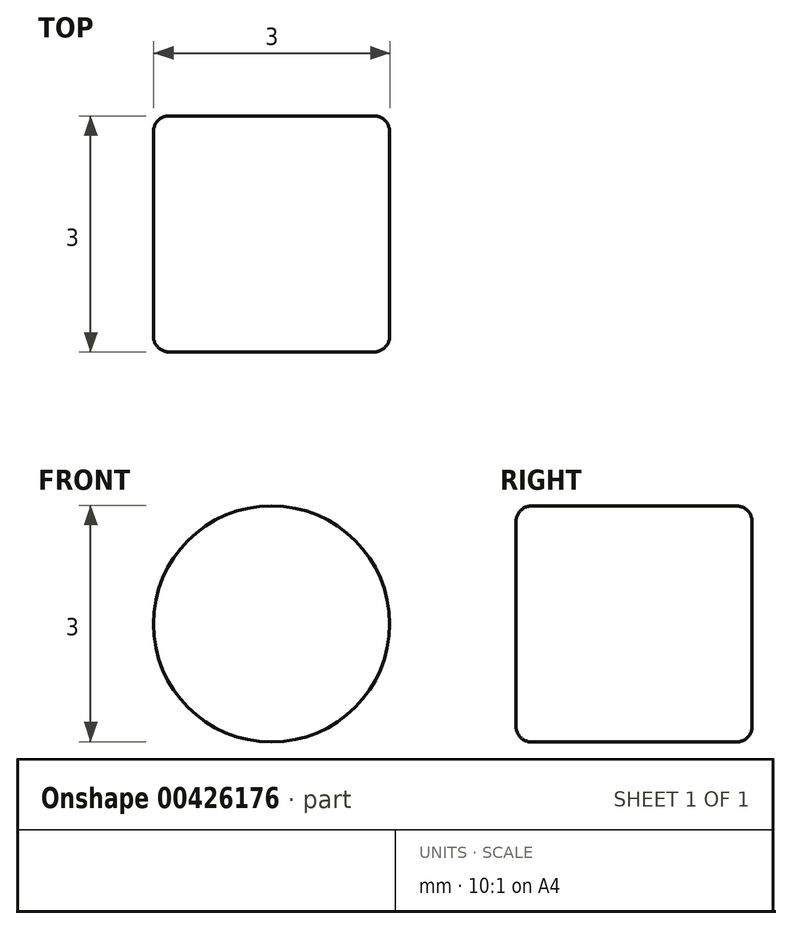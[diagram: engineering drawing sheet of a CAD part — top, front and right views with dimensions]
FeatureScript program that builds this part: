
annotation { "Feature Type Name" : "Feature", "Feature Type Description" : "" }
export const myFeature = defineFeature(function(context is Context, id is Id, definition is map)
    precondition{}
    {
        {
            var Q0;
            Q0=qCreatedBy(makeId("Front.planeOp"),FACE);
            var sketch = newSketch(context, id + "F0", { "sketchPlane" : qUnion([Q0])});
            skCircle(sketch, "E0", {"center": v(-5.4, 45.42) * mm, "radius": 1.5 * mm});
            skCircle(sketch, "E1", {"center": v(-26.87, 2.37) * mm, "radius": 1.5 * mm});
            skCircle(sketch, "E2", {"center": v(-18.87, 2.37) * mm, "radius": 1.5 * mm});
            skCircle(sketch, "E3", {"center": v(-8.9, 45.42) * mm, "radius": 1.5 * mm});
            skCircle(sketch, "E4", {"center": v(-12.4, 45.42) * mm, "radius": 1.5 * mm});
            skLineSegment(sketch, "E5", {"start": v(-28.2, 0) * mm, "end": v(-17.78, 0) * mm});
            skLineSegment(sketch, "E6", {"start": v(-29.7, 1.5) * mm, "end": v(-29.7, 15.65) * mm});
            skLineSegment(sketch, "E7", {"start": v(-26.81, 30.44) * mm, "end": v(-26.22, 31.9) * mm});
            skLineSegment(sketch, "E8", {"start": v(-20.6, 41.55) * mm, "end": v(-16.06, 47.28) * mm});
            skLineSegment(sketch, "E9", {"start": v(-16.28, 1.5) * mm, "end": v(-16.28, 10.93) * mm});
            skLineSegment(sketch, "E10", {"start": v(-13.7, 48.42) * mm, "end": v(-5.4, 48.42) * mm});
            skArc(sketch, "E11", {"start": v(-16.28, 10.93) * mm, "mid": v(-15.59, 18.3) * mm, "end": v(-13.53, 25.4) * mm});
            skArc(sketch, "E12", {"start": v(-13.53, 25.4) * mm, "mid": v(-11.6, 29.4) * mm, "end": v(-9.22, 33.16) * mm});
            skArc(sketch, "E13", {"start": v(-29.7, 15.65) * mm, "mid": v(-28.97, 23.18) * mm, "end": v(-26.81, 30.44) * mm});
            skArc(sketch, "E14", {"start": v(-26.22, 31.9) * mm, "mid": v(-23.75, 36.93) * mm, "end": v(-20.6, 41.55) * mm});
            skCircle(sketch, "E15", {"center": v(-5.4, 41.42) * mm, "radius": 1.5 * mm});
            skCircle(sketch, "E16", {"center": v(-8.9, 41.42) * mm, "radius": 1.5 * mm});
            skCircle(sketch, "E17", {"center": v(-12.4, 41.42) * mm, "radius": 1.5 * mm});
            skCircle(sketch, "E18", {"center": v(-5.4, 37.42) * mm, "radius": 1.5 * mm});
            skCircle(sketch, "E19", {"center": v(-8.9, 37.42) * mm, "radius": 1.5 * mm});
            skCircle(sketch, "E20", {"center": v(-12.4, 37.42) * mm, "radius": 1.5 * mm});
            skLineSegment(sketch, "E21", {"start": v(-2.4, 45.42) * mm, "end": v(-2.4, 37.42) * mm});
            skLineSegment(sketch, "E22", {"start": v(-5.4, 34.42) * mm, "end": v(-6.78, 34.42) * mm});
            skArc(sketch, "E23", {"start": v(-5.4, 48.42) * mm, "mid": v(-3.28, 47.54) * mm, "end": v(-2.4, 45.42) * mm});
            skArc(sketch, "E24", {"start": v(-2.4, 37.42) * mm, "mid": v(-3.28, 35.3) * mm, "end": v(-5.4, 34.42) * mm});
            skArc(sketch, "E25", {"start": v(-16.06, 47.28) * mm, "mid": v(-15.01, 48.12) * mm, "end": v(-13.7, 48.42) * mm});
            skArc(sketch, "E26", {"start": v(-9.22, 33.16) * mm, "mid": v(-8.15, 34.08) * mm, "end": v(-6.78, 34.42) * mm});
            skArc(sketch, "E27", {"start": v(-29.7, 1.5) * mm, "mid": v(-29.25, 0.44) * mm, "end": v(-28.2, 0) * mm});
            skArc(sketch, "E28", {"start": v(-17.78, 0) * mm, "mid": v(-16.72, 0.44) * mm, "end": v(-16.28, 1.5) * mm});
            skLineSegment(sketch, "E29", {"start": v(-20.28, 9.5) * mm, "end": v(-20.28, 10.93) * mm});
            skLineSegment(sketch, "E30", {"start": v(-24.2, 8) * mm, "end": v(-21.78, 8) * mm});
            skArc(sketch, "E31", {"start": v(-25.7, 9.5) * mm, "mid": v(-25.25, 8.44) * mm, "end": v(-24.2, 8) * mm});
            skArc(sketch, "E32", {"start": v(-21.78, 8) * mm, "mid": v(-20.72, 8.44) * mm, "end": v(-20.28, 9.5) * mm});
            skLineSegment(sketch, "E33", {"start": v(-25.7, 10.93) * mm, "end": v(-25.7, 9.5) * mm});
            skLineSegment(sketch, "E34", {"start": v(-21.78, 12.43) * mm, "end": v(-24.2, 12.43) * mm});
            skArc(sketch, "E35", {"start": v(-20.28, 10.93) * mm, "mid": v(-20.72, 12) * mm, "end": v(-21.78, 12.43) * mm});
            skArc(sketch, "E36", {"start": v(-24.2, 12.43) * mm, "mid": v(-25.25, 12) * mm, "end": v(-25.7, 10.93) * mm});
            skLineSegment(sketch, "E37", {"start": v(-16.01, 29.94) * mm, "end": v(-16.01, 30.49) * mm});
            skLineSegment(sketch, "E38", {"start": v(-19.14, 28.44) * mm, "end": v(-17.51, 28.44) * mm});
            skLineSegment(sketch, "E39", {"start": v(-20.64, 30.49) * mm, "end": v(-20.64, 29.94) * mm});
            skLineSegment(sketch, "E40", {"start": v(-17.51, 31.99) * mm, "end": v(-19.14, 31.99) * mm});
            skLineSegment(sketch, "E41", {"start": v(-19.08, 19.72) * mm, "end": v(-19.08, 20.7) * mm});
            skLineSegment(sketch, "E42", {"start": v(-22.45, 18.22) * mm, "end": v(-20.58, 18.22) * mm});
            skLineSegment(sketch, "E43", {"start": v(-23.95, 20.7) * mm, "end": v(-23.95, 19.72) * mm});
            skLineSegment(sketch, "E44", {"start": v(-20.58, 22.2) * mm, "end": v(-22.45, 22.2) * mm});
            skArc(sketch, "E45.filletArc", {"start": v(-19.14, 31.99) * mm, "mid": v(-20.2, 31.55) * mm, "end": v(-20.64, 30.49) * mm});
            skArc(sketch, "E46.filletArc", {"start": v(-16.01, 30.49) * mm, "mid": v(-16.45, 31.55) * mm, "end": v(-17.51, 31.99) * mm});
            skArc(sketch, "E47.filletArc", {"start": v(-17.51, 28.44) * mm, "mid": v(-16.45, 28.88) * mm, "end": v(-16.01, 29.94) * mm});
            skArc(sketch, "E48.filletArc", {"start": v(-20.64, 29.94) * mm, "mid": v(-20.2, 28.88) * mm, "end": v(-19.14, 28.44) * mm});
            skArc(sketch, "E49.filletArc", {"start": v(-22.45, 22.2) * mm, "mid": v(-23.51, 21.77) * mm, "end": v(-23.95, 20.7) * mm});
            skArc(sketch, "E50.filletArc", {"start": v(-19.08, 20.7) * mm, "mid": v(-19.52, 21.77) * mm, "end": v(-20.58, 22.2) * mm});
            skArc(sketch, "E51.filletArc", {"start": v(-20.58, 18.22) * mm, "mid": v(-19.52, 18.66) * mm, "end": v(-19.08, 19.72) * mm});
            skArc(sketch, "E52.filletArc", {"start": v(-23.95, 19.72) * mm, "mid": v(-23.51, 18.66) * mm, "end": v(-22.45, 18.22) * mm});
            skArc(sketch, "E53.MirrorCS", {"start": v(29.7, 1.5) * mm, "mid": v(29.25, 0.44) * mm, "end": v(28.2, 0) * mm});
            skLineSegment(sketch, "E54.MirrorCS", {"start": v(23.95, 20.7) * mm, "end": v(23.95, 19.72) * mm});
            skArc(sketch, "E55.MirrorCS", {"start": v(22.45, 22.2) * mm, "mid": v(23.51, 21.77) * mm, "end": v(23.95, 20.7) * mm});
            skLineSegment(sketch, "E56.MirrorCS", {"start": v(25.7, 10.93) * mm, "end": v(25.7, 9.5) * mm});
            skLineSegment(sketch, "E57.MirrorCS", {"start": v(16.01, 29.94) * mm, "end": v(16.01, 30.49) * mm});
            skLineSegment(sketch, "E58.MirrorCS", {"start": v(5.4, 34.42) * mm, "end": v(6.78, 34.42) * mm});
            skLineSegment(sketch, "E59.MirrorCS", {"start": v(19.14, 28.44) * mm, "end": v(17.51, 28.44) * mm});
            skLineSegment(sketch, "E60.MirrorCS", {"start": v(20.64, 30.49) * mm, "end": v(20.64, 29.94) * mm});
            skLineSegment(sketch, "E61.MirrorCS", {"start": v(21.78, 12.43) * mm, "end": v(24.2, 12.43) * mm});
            skLineSegment(sketch, "E62.MirrorCS", {"start": v(17.51, 31.99) * mm, "end": v(19.14, 31.99) * mm});
            skLineSegment(sketch, "E63.MirrorCS", {"start": v(19.08, 19.72) * mm, "end": v(19.08, 20.7) * mm});
            skArc(sketch, "E64.MirrorCS", {"start": v(16.06, 47.28) * mm, "mid": v(15.01, 48.12) * mm, "end": v(13.7, 48.42) * mm});
            skLineSegment(sketch, "E65.MirrorCS", {"start": v(22.45, 18.22) * mm, "end": v(20.58, 18.22) * mm});
            skArc(sketch, "E66.MirrorCS", {"start": v(9.22, 33.16) * mm, "mid": v(8.15, 34.08) * mm, "end": v(6.78, 34.42) * mm});
            skArc(sketch, "E67.MirrorCS", {"start": v(19.14, 31.99) * mm, "mid": v(20.2, 31.55) * mm, "end": v(20.64, 30.49) * mm});
            skLineSegment(sketch, "E68.MirrorCS", {"start": v(26.81, 30.44) * mm, "end": v(26.22, 31.9) * mm});
            skLineSegment(sketch, "E69.MirrorCS", {"start": v(20.28, 9.5) * mm, "end": v(20.28, 10.93) * mm});
            skLineSegment(sketch, "E70.MirrorCS", {"start": v(20.58, 22.2) * mm, "end": v(22.45, 22.2) * mm});
            skArc(sketch, "E71.MirrorCS", {"start": v(17.78, 0) * mm, "mid": v(16.72, 0.44) * mm, "end": v(16.28, 1.5) * mm});
            skArc(sketch, "E72.MirrorCS", {"start": v(16.01, 30.49) * mm, "mid": v(16.45, 31.55) * mm, "end": v(17.51, 31.99) * mm});
            skLineSegment(sketch, "E73.MirrorCS", {"start": v(24.2, 8) * mm, "end": v(21.78, 8) * mm});
            skArc(sketch, "E74.MirrorCS", {"start": v(17.51, 28.44) * mm, "mid": v(16.45, 28.88) * mm, "end": v(16.01, 29.94) * mm});
            skArc(sketch, "E75.MirrorCS", {"start": v(25.7, 9.5) * mm, "mid": v(25.25, 8.44) * mm, "end": v(24.2, 8) * mm});
            skArc(sketch, "E76.MirrorCS", {"start": v(24.2, 12.43) * mm, "mid": v(25.25, 12) * mm, "end": v(25.7, 10.93) * mm});
            skArc(sketch, "E77.MirrorCS", {"start": v(20.28, 10.93) * mm, "mid": v(20.72, 12) * mm, "end": v(21.78, 12.43) * mm});
            skArc(sketch, "E78.MirrorCS", {"start": v(20.64, 29.94) * mm, "mid": v(20.2, 28.88) * mm, "end": v(19.14, 28.44) * mm});
            skArc(sketch, "E79.MirrorCS", {"start": v(23.95, 19.72) * mm, "mid": v(23.51, 18.66) * mm, "end": v(22.45, 18.22) * mm});
            skArc(sketch, "E80.MirrorCS", {"start": v(21.78, 8) * mm, "mid": v(20.72, 8.44) * mm, "end": v(20.28, 9.5) * mm});
            skCircle(sketch, "E81.MirrorC", {"center": v(12.4, 41.42) * mm, "radius": 1.5 * mm});
            skLineSegment(sketch, "E82.MirrorCS", {"start": v(2.4, 45.42) * mm, "end": v(2.4, 37.42) * mm});
            skCircle(sketch, "E83.MirrorC", {"center": v(5.4, 37.42) * mm, "radius": 1.5 * mm});
            skArc(sketch, "E84.MirrorCS", {"start": v(19.08, 20.7) * mm, "mid": v(19.52, 21.77) * mm, "end": v(20.58, 22.2) * mm});
            skArc(sketch, "E85.MirrorCS", {"start": v(5.4, 48.42) * mm, "mid": v(3.28, 47.54) * mm, "end": v(2.4, 45.42) * mm});
            skArc(sketch, "E86.MirrorCS", {"start": v(2.4, 37.42) * mm, "mid": v(3.28, 35.3) * mm, "end": v(5.4, 34.42) * mm});
            skLineSegment(sketch, "E87.MirrorCS", {"start": v(29.7, 1.5) * mm, "end": v(29.7, 15.65) * mm});
            skLineSegment(sketch, "E88.MirrorCS", {"start": v(20.6, 41.55) * mm, "end": v(16.06, 47.28) * mm});
            skLineSegment(sketch, "E89.MirrorCS", {"start": v(16.28, 1.5) * mm, "end": v(16.28, 10.93) * mm});
            skLineSegment(sketch, "E90.MirrorCS", {"start": v(13.7, 48.42) * mm, "end": v(5.4, 48.42) * mm});
            skArc(sketch, "E91.MirrorCS", {"start": v(29.7, 15.65) * mm, "mid": v(28.97, 23.18) * mm, "end": v(26.81, 30.44) * mm});
            skArc(sketch, "E92.MirrorCS", {"start": v(26.22, 31.9) * mm, "mid": v(23.75, 36.93) * mm, "end": v(20.6, 41.55) * mm});
            skCircle(sketch, "E93.MirrorC", {"center": v(5.4, 41.42) * mm, "radius": 1.5 * mm});
            skArc(sketch, "E94.MirrorCS", {"start": v(16.28, 10.93) * mm, "mid": v(15.59, 18.3) * mm, "end": v(13.53, 25.4) * mm});
            skCircle(sketch, "E95.MirrorC", {"center": v(5.4, 45.42) * mm, "radius": 1.5 * mm});
            skCircle(sketch, "E96.MirrorC", {"center": v(26.87, 2.37) * mm, "radius": 1.5 * mm});
            skArc(sketch, "E97.MirrorCS", {"start": v(13.53, 25.4) * mm, "mid": v(11.6, 29.4) * mm, "end": v(9.22, 33.16) * mm});
            skCircle(sketch, "E98.MirrorC", {"center": v(18.87, 2.37) * mm, "radius": 1.5 * mm});
            skCircle(sketch, "E99.MirrorC", {"center": v(8.9, 45.42) * mm, "radius": 1.5 * mm});
            skCircle(sketch, "E100.MirrorC", {"center": v(12.4, 45.42) * mm, "radius": 1.5 * mm});
            skLineSegment(sketch, "E101.MirrorCS", {"start": v(28.2, 0) * mm, "end": v(17.78, 0) * mm});
            skCircle(sketch, "E102.MirrorC", {"center": v(8.9, 41.42) * mm, "radius": 1.5 * mm});
            skCircle(sketch, "E103.MirrorC", {"center": v(8.9, 37.42) * mm, "radius": 1.5 * mm});
            skArc(sketch, "E104.MirrorCS", {"start": v(20.58, 18.22) * mm, "mid": v(19.52, 18.66) * mm, "end": v(19.08, 19.72) * mm});
            skCircle(sketch, "E105.MirrorC", {"center": v(12.4, 37.42) * mm, "radius": 1.5 * mm});
            skSolve(sketch);
        }
        {
            var Q0;
            Q0=makeQuery(id+"F0.imprint","IMPRINT",FACE,{"disambiguationData":[TD([[makeQuery(id+"F0.imprint","IMPRINT",EDGE,{"derivedFrom":sQuery(id+"F0.wireOp",EDGE,"E0")}),1.0]])]});
            var Q1;
            Q1=makeQuery(id+"F0.imprint","IMPRINT",FACE,{"disambiguationData":[TD([[makeQuery(id+"F0.imprint","IMPRINT",EDGE,{"derivedFrom":sQuery(id+"F0.wireOp",EDGE,"E53.MirrorCS")}),-1.0]])]});
            extrude(context, id + "F1", {"entities" : qUnion([Q0, Q1]), "depth" : 3 * mm});
        }
        {
            var Q0;
            Q0=makeQuery(id+"F1.opExtrude","CAP_FACE",FACE,{"disambiguationData":[OSD([sQuery(id+"F0.wireOp",EDGE,"E0"),sQuery(id+"F0.wireOp",EDGE,"E1"),sQuery(id+"F0.wireOp",EDGE,"E2"),sQuery(id+"F0.wireOp",EDGE,"E3"),sQuery(id+"F0.wireOp",EDGE,"E4"),sQuery(id+"F0.wireOp",EDGE,"E5"),sQuery(id+"F0.wireOp",EDGE,"E6"),sQuery(id+"F0.wireOp",EDGE,"E7"),sQuery(id+"F0.wireOp",EDGE,"E8"),sQuery(id+"F0.wireOp",EDGE,"E9"),sQuery(id+"F0.wireOp",EDGE,"E10"),sQuery(id+"F0.wireOp",EDGE,"E11"),sQuery(id+"F0.wireOp",EDGE,"E12"),sQuery(id+"F0.wireOp",EDGE,"E13"),sQuery(id+"F0.wireOp",EDGE,"E14"),sQuery(id+"F0.wireOp",EDGE,"E15"),sQuery(id+"F0.wireOp",EDGE,"E16"),sQuery(id+"F0.wireOp",EDGE,"E17"),sQuery(id+"F0.wireOp",EDGE,"E18"),sQuery(id+"F0.wireOp",EDGE,"E19"),sQuery(id+"F0.wireOp",EDGE,"E20"),sQuery(id+"F0.wireOp",EDGE,"E21"),sQuery(id+"F0.wireOp",EDGE,"E22"),sQuery(id+"F0.wireOp",EDGE,"E23"),sQuery(id+"F0.wireOp",EDGE,"E24"),sQuery(id+"F0.wireOp",EDGE,"E25"),sQuery(id+"F0.wireOp",EDGE,"E26"),sQuery(id+"F0.wireOp",EDGE,"E27"),sQuery(id+"F0.wireOp",EDGE,"E28"),sQuery(id+"F0.wireOp",EDGE,"E29"),sQuery(id+"F0.wireOp",EDGE,"E30"),sQuery(id+"F0.wireOp",EDGE,"E31"),sQuery(id+"F0.wireOp",EDGE,"E32"),sQuery(id+"F0.wireOp",EDGE,"E33"),sQuery(id+"F0.wireOp",EDGE,"E34"),sQuery(id+"F0.wireOp",EDGE,"E35"),sQuery(id+"F0.wireOp",EDGE,"E36"),sQuery(id+"F0.wireOp",EDGE,"E37"),sQuery(id+"F0.wireOp",EDGE,"E38"),sQuery(id+"F0.wireOp",EDGE,"E39"),sQuery(id+"F0.wireOp",EDGE,"E40"),sQuery(id+"F0.wireOp",EDGE,"E41"),sQuery(id+"F0.wireOp",EDGE,"E42"),sQuery(id+"F0.wireOp",EDGE,"E43"),sQuery(id+"F0.wireOp",EDGE,"E44"),sQuery(id+"F0.wireOp",EDGE,"E45.filletArc"),sQuery(id+"F0.wireOp",EDGE,"E46.filletArc"),sQuery(id+"F0.wireOp",EDGE,"E47.filletArc"),sQuery(id+"F0.wireOp",EDGE,"E48.filletArc"),sQuery(id+"F0.wireOp",EDGE,"E49.filletArc"),sQuery(id+"F0.wireOp",EDGE,"E50.filletArc"),sQuery(id+"F0.wireOp",EDGE,"E51.filletArc"),sQuery(id+"F0.wireOp",EDGE,"E52.filletArc")])],"isStart":false});
            var Q1;
            Q1=makeQuery(id+"F1.opExtrude","CAP_FACE",FACE,{"disambiguationData":[OSD([sQuery(id+"F0.wireOp",EDGE,"E53.MirrorCS"),sQuery(id+"F0.wireOp",EDGE,"E54.MirrorCS"),sQuery(id+"F0.wireOp",EDGE,"E55.MirrorCS"),sQuery(id+"F0.wireOp",EDGE,"E56.MirrorCS"),sQuery(id+"F0.wireOp",EDGE,"E57.MirrorCS"),sQuery(id+"F0.wireOp",EDGE,"E58.MirrorCS"),sQuery(id+"F0.wireOp",EDGE,"E59.MirrorCS"),sQuery(id+"F0.wireOp",EDGE,"E60.MirrorCS"),sQuery(id+"F0.wireOp",EDGE,"E61.MirrorCS"),sQuery(id+"F0.wireOp",EDGE,"E62.MirrorCS"),sQuery(id+"F0.wireOp",EDGE,"E63.MirrorCS"),sQuery(id+"F0.wireOp",EDGE,"E64.MirrorCS"),sQuery(id+"F0.wireOp",EDGE,"E65.MirrorCS"),sQuery(id+"F0.wireOp",EDGE,"E66.MirrorCS"),sQuery(id+"F0.wireOp",EDGE,"E67.MirrorCS"),sQuery(id+"F0.wireOp",EDGE,"E68.MirrorCS"),sQuery(id+"F0.wireOp",EDGE,"E69.MirrorCS"),sQuery(id+"F0.wireOp",EDGE,"E70.MirrorCS"),sQuery(id+"F0.wireOp",EDGE,"E71.MirrorCS"),sQuery(id+"F0.wireOp",EDGE,"E72.MirrorCS"),sQuery(id+"F0.wireOp",EDGE,"E73.MirrorCS"),sQuery(id+"F0.wireOp",EDGE,"E74.MirrorCS"),sQuery(id+"F0.wireOp",EDGE,"E75.MirrorCS"),sQuery(id+"F0.wireOp",EDGE,"E76.MirrorCS"),sQuery(id+"F0.wireOp",EDGE,"E77.MirrorCS"),sQuery(id+"F0.wireOp",EDGE,"E78.MirrorCS"),sQuery(id+"F0.wireOp",EDGE,"E79.MirrorCS"),sQuery(id+"F0.wireOp",EDGE,"E80.MirrorCS"),sQuery(id+"F0.wireOp",EDGE,"E81.MirrorC"),sQuery(id+"F0.wireOp",EDGE,"E82.MirrorCS"),sQuery(id+"F0.wireOp",EDGE,"E83.MirrorC"),sQuery(id+"F0.wireOp",EDGE,"E84.MirrorCS"),sQuery(id+"F0.wireOp",EDGE,"E85.MirrorCS"),sQuery(id+"F0.wireOp",EDGE,"E86.MirrorCS"),sQuery(id+"F0.wireOp",EDGE,"E87.MirrorCS"),sQuery(id+"F0.wireOp",EDGE,"E88.MirrorCS"),sQuery(id+"F0.wireOp",EDGE,"E89.MirrorCS"),sQuery(id+"F0.wireOp",EDGE,"E90.MirrorCS"),sQuery(id+"F0.wireOp",EDGE,"E91.MirrorCS"),sQuery(id+"F0.wireOp",EDGE,"E92.MirrorCS"),sQuery(id+"F0.wireOp",EDGE,"E93.MirrorC"),sQuery(id+"F0.wireOp",EDGE,"E94.MirrorCS"),sQuery(id+"F0.wireOp",EDGE,"E95.MirrorC"),sQuery(id+"F0.wireOp",EDGE,"E96.MirrorC"),sQuery(id+"F0.wireOp",EDGE,"E97.MirrorCS"),sQuery(id+"F0.wireOp",EDGE,"E98.MirrorC"),sQuery(id+"F0.wireOp",EDGE,"E99.MirrorC"),sQuery(id+"F0.wireOp",EDGE,"E100.MirrorC"),sQuery(id+"F0.wireOp",EDGE,"E101.MirrorCS"),sQuery(id+"F0.wireOp",EDGE,"E102.MirrorC"),sQuery(id+"F0.wireOp",EDGE,"E103.MirrorC"),sQuery(id+"F0.wireOp",EDGE,"E104.MirrorCS"),sQuery(id+"F0.wireOp",EDGE,"E105.MirrorC")])],"isStart":false});
            fillet(context, id + "F2", {"entities" : qUnion([Q0, Q1]), "radius" : .2 * mm, "tangentPropagation" : true, "allowEdgeOverflow" : false});
        }
        {
            var Q0;
            Q0=makeQuery(id+"F1.opExtrude","CAP_FACE",FACE,{"disambiguationData":[OSD([sQuery(id+"F0.wireOp",EDGE,"E0"),sQuery(id+"F0.wireOp",EDGE,"E1"),sQuery(id+"F0.wireOp",EDGE,"E2"),sQuery(id+"F0.wireOp",EDGE,"E3"),sQuery(id+"F0.wireOp",EDGE,"E4"),sQuery(id+"F0.wireOp",EDGE,"E5"),sQuery(id+"F0.wireOp",EDGE,"E6"),sQuery(id+"F0.wireOp",EDGE,"E7"),sQuery(id+"F0.wireOp",EDGE,"E8"),sQuery(id+"F0.wireOp",EDGE,"E9"),sQuery(id+"F0.wireOp",EDGE,"E10"),sQuery(id+"F0.wireOp",EDGE,"E11"),sQuery(id+"F0.wireOp",EDGE,"E12"),sQuery(id+"F0.wireOp",EDGE,"E13"),sQuery(id+"F0.wireOp",EDGE,"E14"),sQuery(id+"F0.wireOp",EDGE,"E15"),sQuery(id+"F0.wireOp",EDGE,"E16"),sQuery(id+"F0.wireOp",EDGE,"E17"),sQuery(id+"F0.wireOp",EDGE,"E18"),sQuery(id+"F0.wireOp",EDGE,"E19"),sQuery(id+"F0.wireOp",EDGE,"E20"),sQuery(id+"F0.wireOp",EDGE,"E21"),sQuery(id+"F0.wireOp",EDGE,"E22"),sQuery(id+"F0.wireOp",EDGE,"E23"),sQuery(id+"F0.wireOp",EDGE,"E24"),sQuery(id+"F0.wireOp",EDGE,"E25"),sQuery(id+"F0.wireOp",EDGE,"E26"),sQuery(id+"F0.wireOp",EDGE,"E27"),sQuery(id+"F0.wireOp",EDGE,"E28"),sQuery(id+"F0.wireOp",EDGE,"E29"),sQuery(id+"F0.wireOp",EDGE,"E30"),sQuery(id+"F0.wireOp",EDGE,"E31"),sQuery(id+"F0.wireOp",EDGE,"E32"),sQuery(id+"F0.wireOp",EDGE,"E33"),sQuery(id+"F0.wireOp",EDGE,"E34"),sQuery(id+"F0.wireOp",EDGE,"E35"),sQuery(id+"F0.wireOp",EDGE,"E36"),sQuery(id+"F0.wireOp",EDGE,"E37"),sQuery(id+"F0.wireOp",EDGE,"E38"),sQuery(id+"F0.wireOp",EDGE,"E39"),sQuery(id+"F0.wireOp",EDGE,"E40"),sQuery(id+"F0.wireOp",EDGE,"E41"),sQuery(id+"F0.wireOp",EDGE,"E42"),sQuery(id+"F0.wireOp",EDGE,"E43"),sQuery(id+"F0.wireOp",EDGE,"E44"),sQuery(id+"F0.wireOp",EDGE,"E45.filletArc"),sQuery(id+"F0.wireOp",EDGE,"E46.filletArc"),sQuery(id+"F0.wireOp",EDGE,"E47.filletArc"),sQuery(id+"F0.wireOp",EDGE,"E48.filletArc"),sQuery(id+"F0.wireOp",EDGE,"E49.filletArc"),sQuery(id+"F0.wireOp",EDGE,"E50.filletArc"),sQuery(id+"F0.wireOp",EDGE,"E51.filletArc"),sQuery(id+"F0.wireOp",EDGE,"E52.filletArc")])],"isStart":true});
            var Q1;
            Q1=makeQuery(id+"F1.opExtrude","CAP_FACE",FACE,{"disambiguationData":[OSD([sQuery(id+"F0.wireOp",EDGE,"E53.MirrorCS"),sQuery(id+"F0.wireOp",EDGE,"E54.MirrorCS"),sQuery(id+"F0.wireOp",EDGE,"E55.MirrorCS"),sQuery(id+"F0.wireOp",EDGE,"E56.MirrorCS"),sQuery(id+"F0.wireOp",EDGE,"E57.MirrorCS"),sQuery(id+"F0.wireOp",EDGE,"E58.MirrorCS"),sQuery(id+"F0.wireOp",EDGE,"E59.MirrorCS"),sQuery(id+"F0.wireOp",EDGE,"E60.MirrorCS"),sQuery(id+"F0.wireOp",EDGE,"E61.MirrorCS"),sQuery(id+"F0.wireOp",EDGE,"E62.MirrorCS"),sQuery(id+"F0.wireOp",EDGE,"E63.MirrorCS"),sQuery(id+"F0.wireOp",EDGE,"E64.MirrorCS"),sQuery(id+"F0.wireOp",EDGE,"E65.MirrorCS"),sQuery(id+"F0.wireOp",EDGE,"E66.MirrorCS"),sQuery(id+"F0.wireOp",EDGE,"E67.MirrorCS"),sQuery(id+"F0.wireOp",EDGE,"E68.MirrorCS"),sQuery(id+"F0.wireOp",EDGE,"E69.MirrorCS"),sQuery(id+"F0.wireOp",EDGE,"E70.MirrorCS"),sQuery(id+"F0.wireOp",EDGE,"E71.MirrorCS"),sQuery(id+"F0.wireOp",EDGE,"E72.MirrorCS"),sQuery(id+"F0.wireOp",EDGE,"E73.MirrorCS"),sQuery(id+"F0.wireOp",EDGE,"E74.MirrorCS"),sQuery(id+"F0.wireOp",EDGE,"E75.MirrorCS"),sQuery(id+"F0.wireOp",EDGE,"E76.MirrorCS"),sQuery(id+"F0.wireOp",EDGE,"E77.MirrorCS"),sQuery(id+"F0.wireOp",EDGE,"E78.MirrorCS"),sQuery(id+"F0.wireOp",EDGE,"E79.MirrorCS"),sQuery(id+"F0.wireOp",EDGE,"E80.MirrorCS"),sQuery(id+"F0.wireOp",EDGE,"E81.MirrorC"),sQuery(id+"F0.wireOp",EDGE,"E82.MirrorCS"),sQuery(id+"F0.wireOp",EDGE,"E83.MirrorC"),sQuery(id+"F0.wireOp",EDGE,"E84.MirrorCS"),sQuery(id+"F0.wireOp",EDGE,"E85.MirrorCS"),sQuery(id+"F0.wireOp",EDGE,"E86.MirrorCS"),sQuery(id+"F0.wireOp",EDGE,"E87.MirrorCS"),sQuery(id+"F0.wireOp",EDGE,"E88.MirrorCS"),sQuery(id+"F0.wireOp",EDGE,"E89.MirrorCS"),sQuery(id+"F0.wireOp",EDGE,"E90.MirrorCS"),sQuery(id+"F0.wireOp",EDGE,"E91.MirrorCS"),sQuery(id+"F0.wireOp",EDGE,"E92.MirrorCS"),sQuery(id+"F0.wireOp",EDGE,"E93.MirrorC"),sQuery(id+"F0.wireOp",EDGE,"E94.MirrorCS"),sQuery(id+"F0.wireOp",EDGE,"E95.MirrorC"),sQuery(id+"F0.wireOp",EDGE,"E96.MirrorC"),sQuery(id+"F0.wireOp",EDGE,"E97.MirrorCS"),sQuery(id+"F0.wireOp",EDGE,"E98.MirrorC"),sQuery(id+"F0.wireOp",EDGE,"E99.MirrorC"),sQuery(id+"F0.wireOp",EDGE,"E100.MirrorC"),sQuery(id+"F0.wireOp",EDGE,"E101.MirrorCS"),sQuery(id+"F0.wireOp",EDGE,"E102.MirrorC"),sQuery(id+"F0.wireOp",EDGE,"E103.MirrorC"),sQuery(id+"F0.wireOp",EDGE,"E104.MirrorCS"),sQuery(id+"F0.wireOp",EDGE,"E105.MirrorC")])],"isStart":true});
            fillet(context, id + "F3", {"entities" : qUnion([Q0, Q1]), "radius" : .2 * mm, "tangentPropagation" : true, "allowEdgeOverflow" : false});
        }
    });
